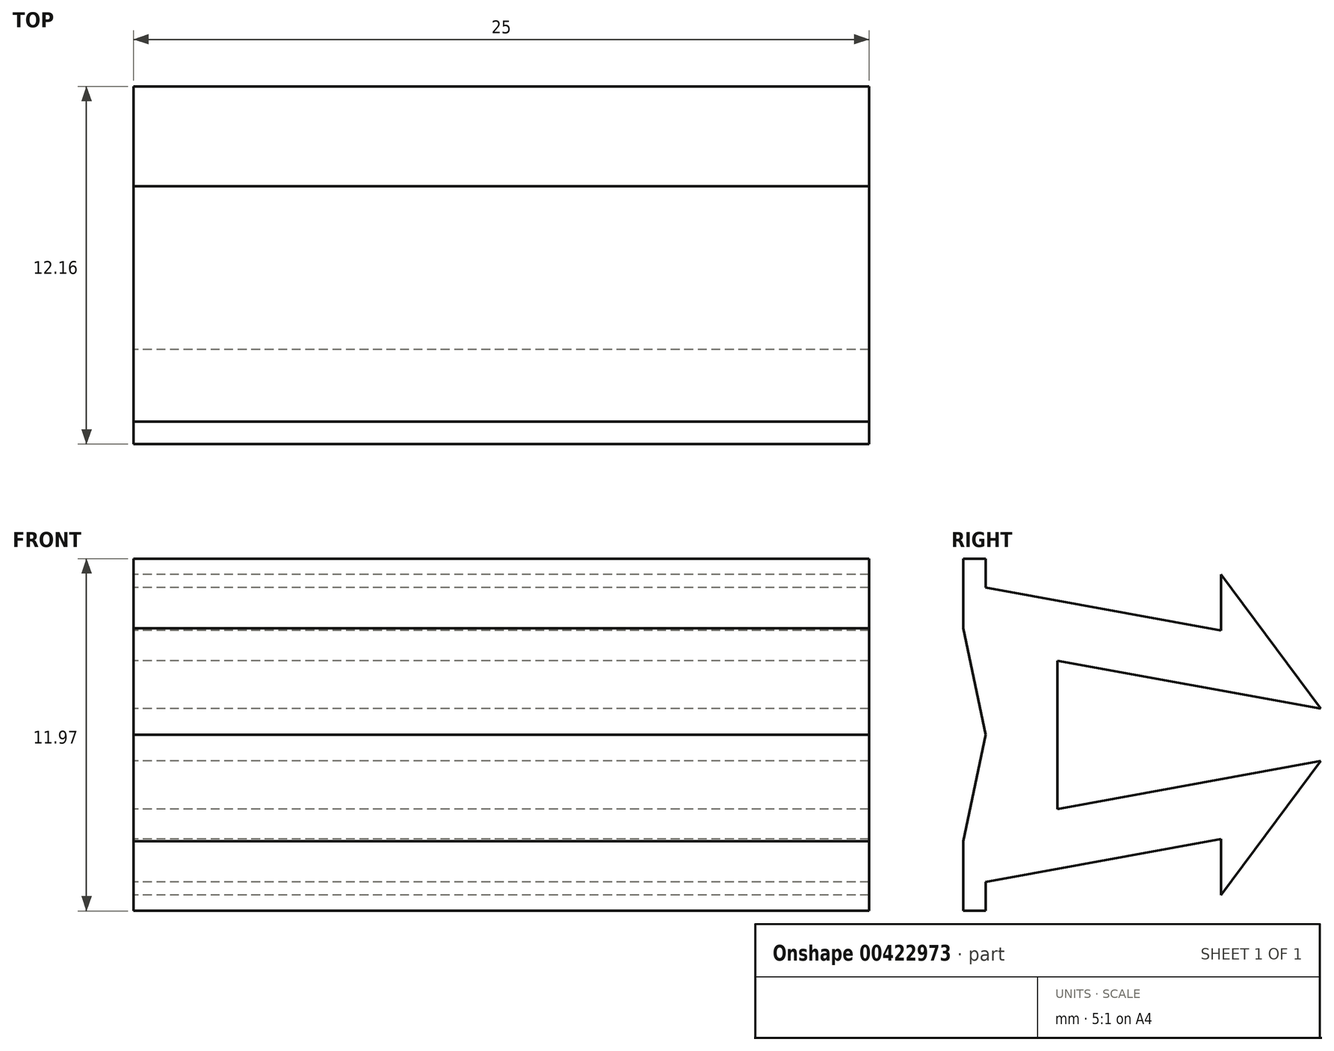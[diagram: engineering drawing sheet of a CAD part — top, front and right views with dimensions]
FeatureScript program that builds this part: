
annotation { "Feature Type Name" : "Feature", "Feature Type Description" : "" }
export const myFeature = defineFeature(function(context is Context, id is Id, definition is map)
    precondition{}
    {
        {
            var Q0;
            Q0=qCreatedBy(makeId("Right.planeOp"),FACE);
            var sketch = newSketch(context, id + "F0", { "sketchPlane" : qUnion([Q0])});
            skLineSegment(sketch, "E0", {"start": v(0, 20.05) * mm, "end": v(8, 18.59) * mm});
            skLineSegment(sketch, "E1", {"start": v(8, 18.59) * mm, "end": v(8, 20.5) * mm});
            skLineSegment(sketch, "E2", {"start": v(8, 20.5) * mm, "end": v(11.4, 15.93) * mm});
            skLineSegment(sketch, "E3", {"start": v(11.4, 15.93) * mm, "end": v(2.45, 17.57) * mm});
            skLineSegment(sketch, "E4", {"start": v(2.45, 17.57) * mm, "end": v(2.45, 15.05) * mm});
            skPoint(sketch, "E5.endSnap0", {"position": v(0, 10.02) * mm});
            skPoint(sketch, "E6.orphan", {"position": v(0, 0) * mm});
            skLineSegment(sketch, "E7", {"start": v(0, 15.05) * mm, "end": v(4.2, 15.05) * mm, "construction": true});
            skLineSegment(sketch, "E8", {"start": v(-0.76, 18.66) * mm, "end": v(-0.76, 21.03) * mm});
            skLineSegment(sketch, "E9", {"start": v(-0.76, 21.03) * mm, "end": v(0, 21.03) * mm});
            skLineSegment(sketch, "E10", {"start": v(0, 21.03) * mm, "end": v(0, 20.05) * mm});
            skLineSegment(sketch, "E11", {"start": v(-0.76, 18.66) * mm, "end": v(0, 15.05) * mm});
            skLineSegment(sketch, "E12.MirrorCS", {"start": v(-0.76, 11.43) * mm, "end": v(0, 15.05) * mm});
            skLineSegment(sketch, "E13.MirrorCS", {"start": v(2.45, 12.53) * mm, "end": v(2.45, 15.05) * mm});
            skLineSegment(sketch, "E14.MirrorCS", {"start": v(8, 9.6) * mm, "end": v(11.4, 14.16) * mm});
            skLineSegment(sketch, "E15.MirrorCS", {"start": v(11.4, 14.16) * mm, "end": v(2.45, 12.53) * mm});
            skLineSegment(sketch, "E16.MirrorCS", {"start": v(-0.76, 9.06) * mm, "end": v(0, 9.06) * mm});
            skLineSegment(sketch, "E17.MirrorCS", {"start": v(-0.76, 11.43) * mm, "end": v(-0.76, 9.06) * mm});
            skLineSegment(sketch, "E18.MirrorCS", {"start": v(0, 10.05) * mm, "end": v(8, 11.5) * mm});
            skLineSegment(sketch, "E19.MirrorCS", {"start": v(0, 9.06) * mm, "end": v(0, 10.05) * mm});
            skLineSegment(sketch, "E20.MirrorCS", {"start": v(8, 11.5) * mm, "end": v(8, 9.6) * mm});
            skSolve(sketch);
        }
        {
            var Q0;
            Q0=makeQuery(id+"F0.imprint","IMPRINT",FACE,{"disambiguationData":[TD([[makeQuery(id+"F0.imprint","IMPRINT",EDGE,{"derivedFrom":sQuery(id+"F0.wireOp",EDGE,"E0")}),-1.0]])]});
            extrude(context, id + "F1", {"entities" : qUnion([Q0]), "depth" : 25 * mm});
        }
    });
